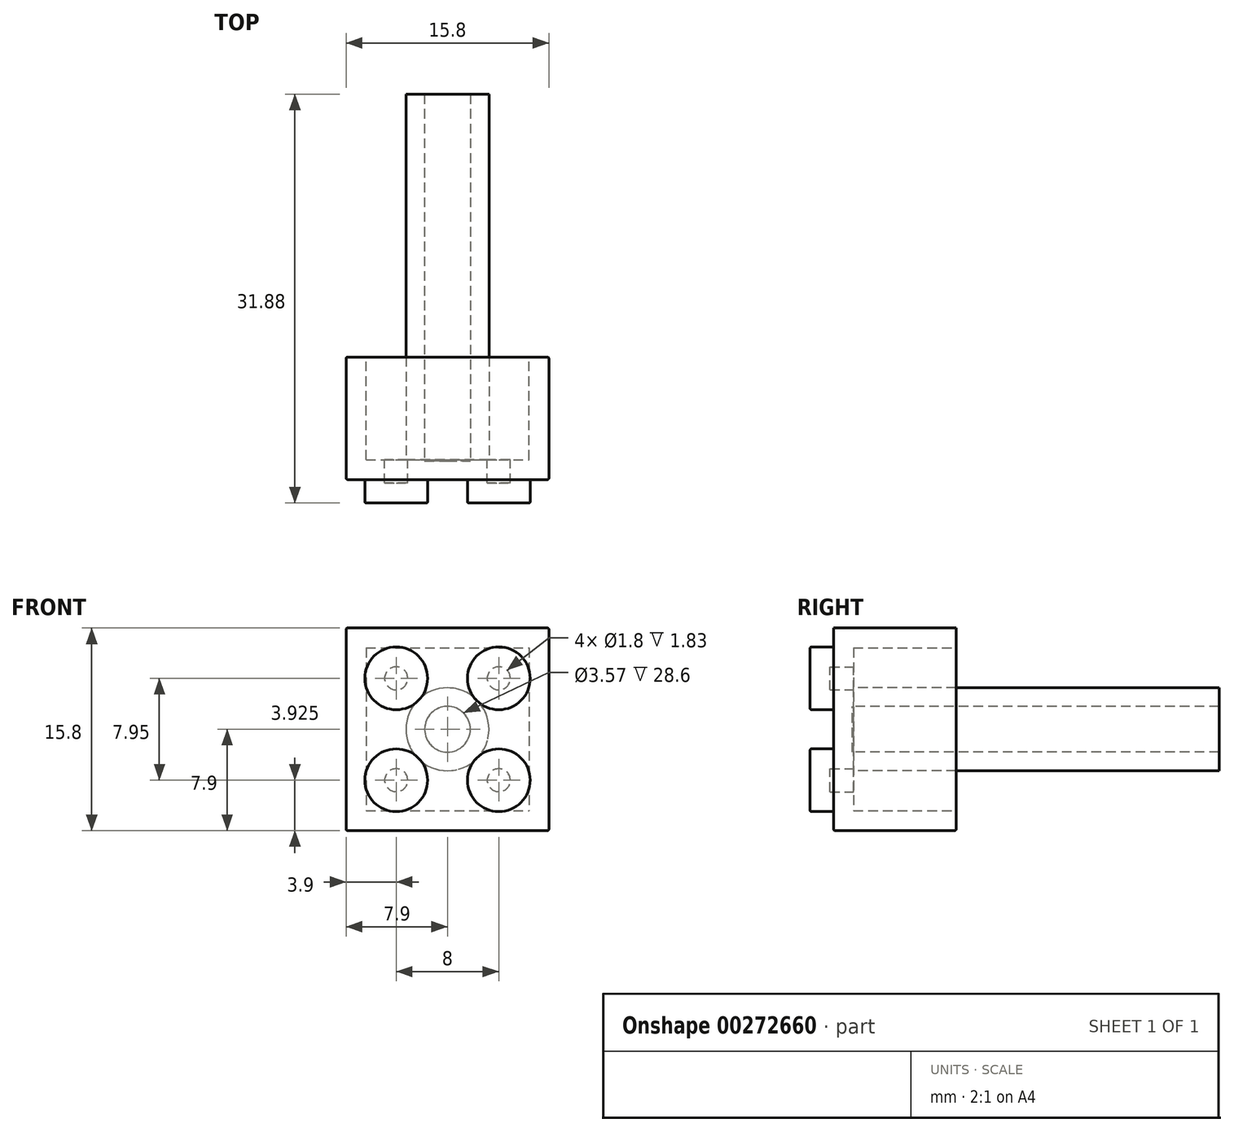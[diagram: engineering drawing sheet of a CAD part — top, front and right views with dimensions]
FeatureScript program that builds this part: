
annotation { "Feature Type Name" : "Feature", "Feature Type Description" : "" }
export const myFeature = defineFeature(function(context is Context, id is Id, definition is map)
    precondition{}
    {
        {
            var Q0;
            Q0=qCreatedBy(makeId("Front.planeOp"),FACE);
            var sketch = newSketch(context, id + "F0", { "sketchPlane" : qUnion([Q0])});
            skLineSegment(sketch, "E0.bottom", {"start": v(0, 0) * mm, "end": v(15.8, 0) * mm});
            skLineSegment(sketch, "E0.top", {"start": v(0, 15.8) * mm, "end": v(15.8, 15.8) * mm});
            skLineSegment(sketch, "E0.left", {"start": v(0, 0) * mm, "end": v(0, 15.8) * mm});
            skLineSegment(sketch, "E0.right", {"start": v(15.8, 0) * mm, "end": v(15.8, 15.8) * mm});
            skSolve(sketch);
        }
        {
            var Q0;
            Q0 = qSketchRegion(id + "F0", true);
            extrude(context, id + "F1", {"entities" : qUnion([Q0]), "depth" : 9.55 * mm});
        }
        {
            var Q0;
            Q0=makeQuery(id+"F1.opExtrude","CAP_FACE",FACE,{"disambiguationData":[OSD([sQuery(id+"F0.wireOp",EDGE,"E0.bottom"),sQuery(id+"F0.wireOp",EDGE,"E0.top"),sQuery(id+"F0.wireOp",EDGE,"E0.left"),sQuery(id+"F0.wireOp",EDGE,"E0.right")])],"isStart":false});
            var sketch = newSketch(context, id + "F2", { "sketchPlane" : qUnion([Q0])});
            skCircle(sketch, "E1", {"center": v(3.9, 11.88) * mm, "radius": 2.45 * mm});
            skCircle(sketch, "E2", {"center": v(11.9, 11.88) * mm, "radius": 2.45 * mm});
            skCircle(sketch, "E3", {"center": v(3.9, 3.93) * mm, "radius": 2.45 * mm});
            skCircle(sketch, "E4", {"center": v(11.9, 3.93) * mm, "radius": 2.45 * mm});
            skSolve(sketch);
        }
        {
            var Q0;
            Q0=makeQuery(id+"F2.imprint","IMPRINT",FACE,{"disambiguationData":[TD([[makeQuery(id+"F2.imprint","IMPRINT",EDGE,{"derivedFrom":sQuery(id+"F2.wireOp",EDGE,"E1")}),1.0]])]});
            var Q1;
            Q1=makeQuery(id+"F2.imprint","IMPRINT",FACE,{"disambiguationData":[TD([[makeQuery(id+"F2.imprint","IMPRINT",EDGE,{"derivedFrom":sQuery(id+"F2.wireOp",EDGE,"E3")}),1.0]])]});
            var Q2;
            Q2=makeQuery(id+"F2.imprint","IMPRINT",FACE,{"disambiguationData":[TD([[makeQuery(id+"F2.imprint","IMPRINT",EDGE,{"derivedFrom":sQuery(id+"F2.wireOp",EDGE,"E4")}),1.0]])]});
            var Q3;
            Q3=makeQuery(id+"F2.imprint","IMPRINT",FACE,{"disambiguationData":[TD([[makeQuery(id+"F2.imprint","IMPRINT",EDGE,{"derivedFrom":sQuery(id+"F2.wireOp",EDGE,"E2")}),1.0]])]});
            extrude(context, id + "F3", {"entities" : qUnion([Q0, Q1, Q2, Q3]), "operationType" : NewBodyOperationType.ADD, "depth" : 1.83 * mm});
        }
        {
            var Q0;
            Q0=makeQuery(id+"F3.opExtrude","CAP_EDGE",EDGE,{"disambiguationData":[OSD([sQuery(id+"F2.wireOp",EDGE,"E4")])],"isStart":false});
            var Q1;
            Q1=makeQuery(id+"F3.opExtrude","CAP_FACE",FACE,{"disambiguationData":[OSD([sQuery(id+"F2.wireOp",EDGE,"E2")])],"isStart":false});
            var Q2;
            Q2=makeQuery(id+"F3.opExtrude","CAP_EDGE",EDGE,{"disambiguationData":[OSD([sQuery(id+"F2.wireOp",EDGE,"E1")])],"isStart":false});
            var Q3;
            Q3=makeQuery(id+"F3.opExtrude","CAP_EDGE",EDGE,{"disambiguationData":[OSD([sQuery(id+"F2.wireOp",EDGE,"E3")])],"isStart":false});
            var Q4;
            Q4=makeQuery(id+"F1.opExtrude","SWEPT_EDGE",EDGE,{"disambiguationData":[OSD([sQuery(id+"F0.wireOp",EDGE,"E0.bottom"),sQuery(id+"F0.wireOp",EDGE,"E0.right")])]});
            var Q5;
            Q5=makeQuery(id+"F1.opExtrude","CAP_EDGE",EDGE,{"disambiguationData":[OSD([sQuery(id+"F0.wireOp",EDGE,"E0.bottom")])],"isStart":false});
            var Q6;
            Q6=makeQuery(id+"F1.opExtrude","SWEPT_EDGE",EDGE,{"disambiguationData":[OSD([sQuery(id+"F0.wireOp",EDGE,"E0.bottom"),sQuery(id+"F0.wireOp",EDGE,"E0.left")])]});
            var Q7;
            Q7=makeQuery(id+"F1.opExtrude","CAP_EDGE",EDGE,{"disambiguationData":[OSD([sQuery(id+"F0.wireOp",EDGE,"E0.bottom")])],"isStart":true});
            var Q8;
            Q8=makeQuery(id+"F1.opExtrude","SWEPT_FACE",FACE,{"disambiguationData":[OSD([sQuery(id+"F0.wireOp",EDGE,"E0.right")])]});
            var Q9;
            Q9=makeQuery(id+"F1.opExtrude","SWEPT_FACE",FACE,{"disambiguationData":[OSD([sQuery(id+"F0.wireOp",EDGE,"E0.left")])]});
            fillet(context, id + "F4", {"entities" : qUnion([Q0, Q1, Q2, Q3, Q4, Q5, Q6, Q7, Q8, Q9]), "radius" : .1 * mm, "tangentPropagation" : true, "allowEdgeOverflow" : false});
        }
        {
            var Q0;
            Q0=makeQuery(id+"F1.opExtrude","CAP_FACE",FACE,{"disambiguationData":[OSD([sQuery(id+"F0.wireOp",EDGE,"E0.bottom"),sQuery(id+"F0.wireOp",EDGE,"E0.top"),sQuery(id+"F0.wireOp",EDGE,"E0.left"),sQuery(id+"F0.wireOp",EDGE,"E0.right")])],"isStart":true});
            shell(context, id + "F5", {"entities" : qUnion([Q0]), "thickness" : 1.55 * mm});
        }
        {
            var Q0;
            Q0=makeQuery(id+"F5.opShell","OFFSET_FACE",FACE,{"disambiguationData":[OSD([sQuery(id+"F0.wireOp",EDGE,"E0.bottom"),sQuery(id+"F0.wireOp",EDGE,"E0.top"),sQuery(id+"F0.wireOp",EDGE,"E0.left"),sQuery(id+"F0.wireOp",EDGE,"E0.right")])]});
            var sketch = newSketch(context, id + "F6", { "sketchPlane" : qUnion([Q0])});
            skCircle(sketch, "E5", {"center": v(-7.9, 7.9) * mm, "radius": 3.23 * mm});
            skPoint(sketch, "E5.centerSnap0", {"position": v(-1.55, 7.9) * mm});
            skPoint(sketch, "E5.centerSnap1", {"position": v(-7.9, 14.25) * mm});
            skSolve(sketch);
        }
        {
            var Q0;
            Q0=makeQuery(id+"F6.imprint","IMPRINT",FACE,{"disambiguationData":[TD([[makeQuery(id+"F6.imprint","IMPRINT",EDGE,{"derivedFrom":sQuery(id+"F6.wireOp",EDGE,"E5")}),1.0]])]});
            extrude(context, id + "F7", {"entities" : qUnion([Q0]), "operationType" : NewBodyOperationType.ADD, "depth" : 14.25 * mm});
        }
        {
            var Q0;
            Q0=makeQuery(id+"F7.opExtrude","CAP_FACE",FACE,{"disambiguationData":[OSD([sQuery(id+"F6.wireOp",EDGE,"E5")])],"isStart":false});
            extrude(context, id + "F8", {"entities" : qUnion([Q0]), "operationType" : NewBodyOperationType.ADD, "depth" : 14.25 * mm});
        }
        {
            var Q0;
            Q0=makeQuery(id+"F8.opExtrude","CAP_FACE",FACE,{"disambiguationData":[OSD([sQuery(id+"F6.wireOp",EDGE,"E5")])],"isStart":false});
            shell(context, id + "F9", {"entities" : qUnion([Q0]), "thickness" : 1.45 * mm});
        }
    });
